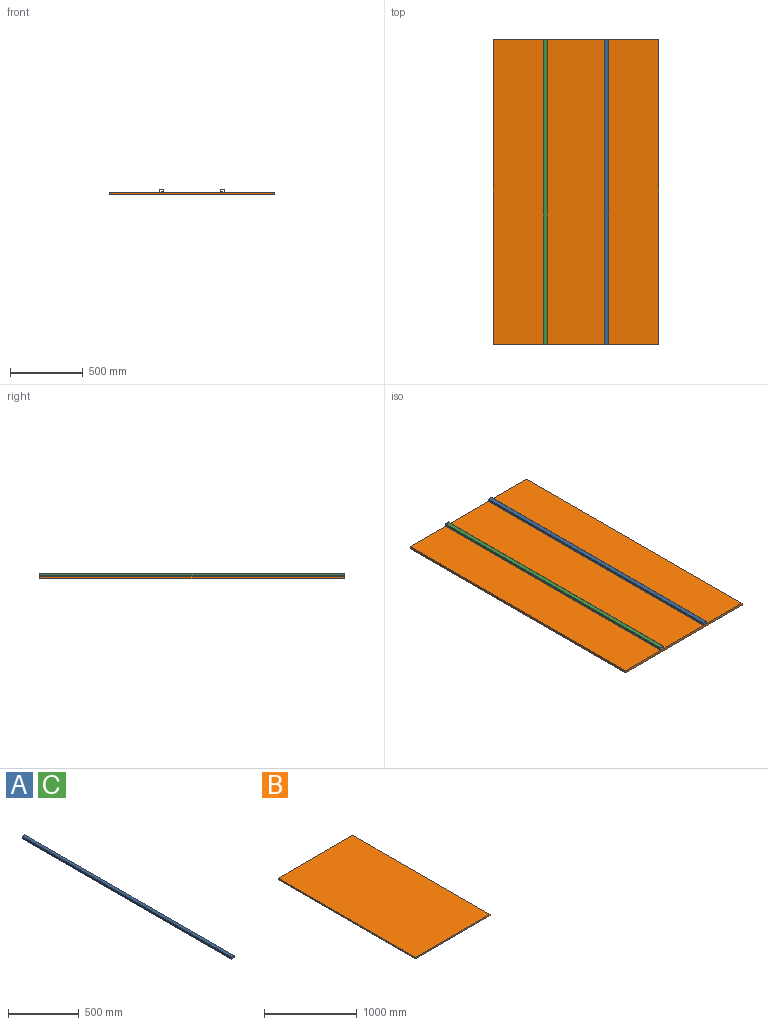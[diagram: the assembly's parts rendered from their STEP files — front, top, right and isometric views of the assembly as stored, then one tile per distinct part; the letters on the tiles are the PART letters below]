
ASSEMBLY  parts=3 mates=2
PART A: 10 faces, bbox 30x2095x20 mm
  f0: plane 30x20mm, normal (0,1,0), area 184mm2, adj f2,f3,f4,f5,f6,f7,f8,f9
  f1: plane 30x20mm, normal (0,-1,0), area 184mm2, adj f2,f3,f4,f5,f6,f7,f8,f9
  f2: plane 2095x20mm, normal (-1,0,0), area 41900mm2, adj f0,f1,f4,f5
  f3: plane 2095x20mm, normal (1,0,0), area 41900mm2, adj f0,f1,f4,f5
  f4: plane 2095x30mm, normal (0,0,1), area 62850mm2, adj f0,f1,f2,f3
  f5: plane 2095x30mm, normal (0,0,-1), area 62850mm2, adj f0,f1,f2,f3
  f6: plane 2095x26mm, normal (0,0,-1), area 54470mm2, adj f0,f1,f7,f9
  f7: plane 2095x16mm, normal (1,0,0), area 33520mm2, adj f0,f1,f6,f8
  f8: plane 2095x26mm, normal (0,0,1), area 54470mm2, adj f0,f1,f7,f9
  f9: plane 2095x16mm, normal (-1,0,0), area 33520mm2, adj f0,f1,f6,f8
PART B: 6 faces, bbox 1140x2095x18 mm
  f0: plane 2095x18mm, normal (-1,0,0), area 37710mm2, adj f1,f3,f4,f5
  f1: plane 1140x18mm, normal (0,-1,0), area 20520mm2, adj f0,f2,f4,f5
  f2: plane 2095x18mm, normal (1,0,0), area 37710mm2, adj f1,f3,f4,f5
  f3: plane 1140x18mm, normal (0,1,0), area 20520mm2, adj f0,f2,f4,f5
  f4: plane 2095x1140mm, normal (0,0,-1), area 2388300mm2, adj f0,f1,f2,f3
  f5: plane 2095x1140mm, normal (0,0,1), area 2388300mm2, adj f0,f1,f2,f3
PART C: same geometry as A
PLACE A t=(194,-749.5,-10)mm
PLACE B t=(0,0,-10)mm
PLACE C t=(-224,-749.5,-10)mm
MATE planar A.f5 <-> B.f5  axis (0,0,-1) through (194,1047.5,-10)mm
MATE planar C.f5 <-> B.f5  axis (0,0,-1) through (-209,0,-10)mm
